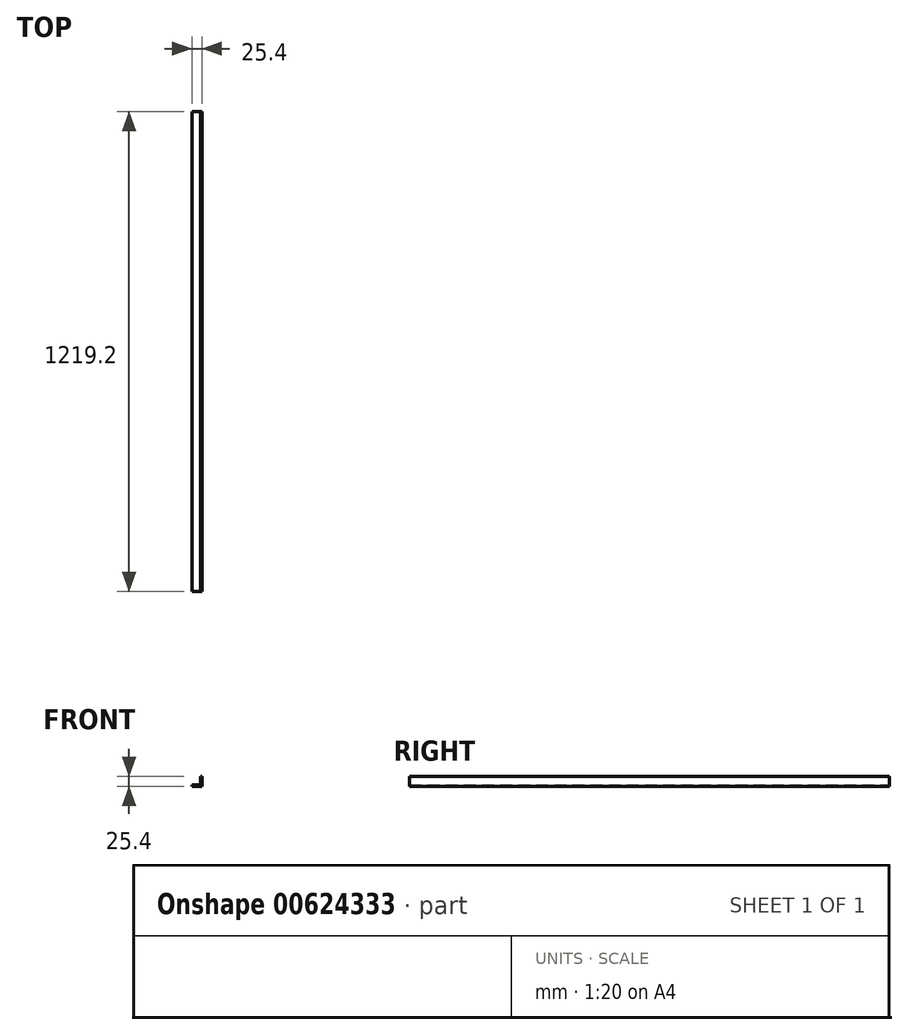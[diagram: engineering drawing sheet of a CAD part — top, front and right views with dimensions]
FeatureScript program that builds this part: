
annotation { "Feature Type Name" : "Feature", "Feature Type Description" : "" }
export const myFeature = defineFeature(function(context is Context, id is Id, definition is map)
    precondition{}
    {
        {
            var Q0;
            Q0=qCreatedBy(makeId("Front.planeOp"),FACE);
            var sketch = newSketch(context, id + "F0", { "sketchPlane" : qUnion([Q0])});
            skLineSegment(sketch, "E0", {"start": v(0, 0) * mm, "end": v(0, 25.4) * mm});
            skLineSegment(sketch, "E1", {"start": v(0, 25.4) * mm, "end": v(-3.25, 25.4) * mm});
            skLineSegment(sketch, "E2", {"start": v(-3.25, 25.4) * mm, "end": v(-3.25, 3.25) * mm});
            skLineSegment(sketch, "E3", {"start": v(-3.25, 3.25) * mm, "end": v(-25.4, 3.25) * mm});
            skLineSegment(sketch, "E4", {"start": v(-25.4, 3.25) * mm, "end": v(-25.4, 0) * mm});
            skLineSegment(sketch, "E5", {"start": v(-25.4, 0) * mm, "end": v(0, 0) * mm});
            skSolve(sketch);
        }
        {
            var Q0;
            Q0=makeQuery(id+"F0.imprint","IMPRINT",FACE,{"disambiguationData":[TD([[makeQuery(id+"F0.imprint","IMPRINT",EDGE,{"derivedFrom":sQuery(id+"F0.wireOp",EDGE,"E0")}),1.0]])]});
            extrude(context, id + "F1", {"entities" : qUnion([Q0]), "endBound" : BoundingType.SYMMETRIC, "depth" : 1219.2 * mm, "offsetDistance" : 25.4 * mm});
        }
    });
